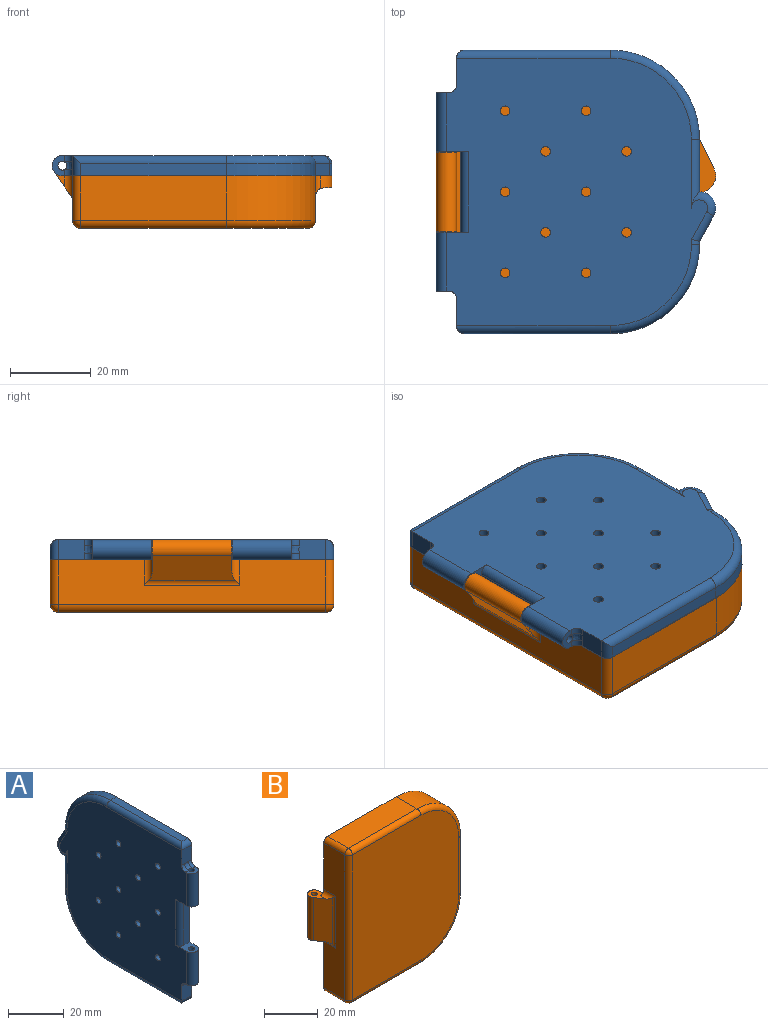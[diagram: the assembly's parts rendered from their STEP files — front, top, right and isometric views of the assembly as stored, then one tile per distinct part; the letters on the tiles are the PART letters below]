
ASSEMBLY  parts=2 mates=1
PART A: 78 faces, bbox 5.4x69.3x73.6 mm
  f0: plane 13x3mm, normal (0,1,0), area 39mm2, adj f1,f10,f59,f67
  f1: plane 70x66.5mm, normal (1,0,0), area 587.2mm2, adj f0,f3,f4,f5,f8,f9,f10,f11
  f2: plane 66x64.5mm, normal (-1,0,0), area 3648.1mm2, adj f3,f4,f40,f41,f42,f43,f44,f45
  f3: cylinder r=2.5mm len=14.5mm, axis (0,0,1), area 113.9mm2, adj f1,f2,f50,f54
  f4: cylinder r=2.5mm len=14.5mm, axis (0,0,1), area 113.9mm2, adj f1,f2,f51,f56
  f5: plane 3x1mm, normal (0,-1,0), area 3mm2, adj f1,f16,f21,f33
  f6: plane 62x52mm, normal (1,0,0), area 2899.7mm2, adj f7,f19,f20,f21,f22,f23,f24,f35
  f7: cylinder r=2mm len=3mm, axis (0,0,1), area 9.4mm2, adj f6,f17,f19,f38
  f8: plane 36x3mm, normal (0,0,1), area 108mm2, adj f1,f12,f61,f62
  f9: plane 36x3mm, normal (0,0,-1), area 108mm2, adj f1,f10,f68,f70
  f10: cylinder r=22mm len=22mm, axis (1,0,0), area 103.7mm2, adj f0,f1,f9,f69
  f11: plane 3x0.74mm, normal (0,1,0), area 2.2mm2, adj f1,f12,f60,f64
  f12: cylinder r=22mm len=22mm, axis (1,0,0), area 103.7mm2, adj f1,f8,f11,f63
  f13: plane 36x1mm, normal (0,0,-1), area 36mm2, adj f1,f14,f18,f20
  f14: plane 66x1mm, normal (0,1,0), area 66mm2, adj f1,f13,f15,f22
  f15: plane 36x1mm, normal (0,0,1), area 36mm2, adj f1,f14,f16,f24
  f16: cylinder r=20mm len=20mm, axis (1,0,0), area 31.4mm2, adj f1,f5,f15,f23
  f17: plane 3x1mm, normal (0,-1,0), area 3mm2, adj f1,f7,f18,f39
  f18: cylinder r=20mm len=20mm, axis (1,0,0), area 31.4mm2, adj f1,f13,f17,f19
  f19: torus R=18mm, axis (1,0,0), area 95.1mm2, adj f6,f7,f18,f20
  f20: cylinder r=2mm len=36mm, axis (0,-1,0), area 110.8mm2, adj f6,f13,f19,f22
  f21: cylinder r=2mm len=3mm, axis (0,0,1), area 9.4mm2, adj f5,f6,f23,f34
  f22: cylinder r=2mm len=66mm, axis (0,0,-1), area 202.8mm2, adj f6,f14,f20,f24
  f23: torus R=18mm, axis (1,0,0), area 95.1mm2, adj f6,f16,f21,f24
  f24: cylinder r=2mm len=36mm, axis (0,1,0), area 110.8mm2, adj f6,f15,f22,f23
  f25: plane 5x1mm, normal (0,0,-1), area 5mm2, adj f1,f26,f33,f35
  f26: plane 16x1mm, normal (0,-1,0), area 16mm2, adj f1,f25,f27,f36
  f27: plane 5x1mm, normal (0,0,1), area 5mm2, adj f1,f26,f37,f39
  f28: plane 6x3.5mm, normal (0,0,-1), area 21mm2, adj f1,f29,f31,f32
  f29: plane 13x3.5mm, normal (0,1,0), area 45.5mm2, adj f1,f28,f30,f32
  f30: plane 6x3.5mm, normal (0,0,1), area 21mm2, adj f1,f29,f31,f32
  f31: plane 13x3.5mm, normal (0,-1,0), area 45.5mm2, adj f1,f28,f30,f32
  f32: plane 13x6mm, normal (1,0,0), area 78mm2, adj f28,f29,f30,f31
  f33: cylinder r=2mm len=2mm, axis (-1,0,0), area 3.1mm2, adj f1,f5,f25,f34
  f34: sphere r=2mm, area 6.3mm2, adj f21,f33,f35
  f35: cylinder r=2mm len=7mm, axis (0,1,0), area 18mm2, adj f6,f25,f34,f36
  f36: cylinder r=2mm len=20mm, axis (0,0,-1), area 54.8mm2, adj f6,f26,f35,f37
  f37: cylinder r=2mm len=7mm, axis (0,-1,0), area 18mm2, adj f6,f27,f36,f38
  f38: sphere r=2mm, area 6.3mm2, adj f7,f37,f39
  f39: cylinder r=2mm len=2mm, axis (1,0,0), area 3.1mm2, adj f1,f17,f27,f38
  f40: cylinder r=1.2mm len=2.4mm, axis (1,0,0), area 15.1mm2, adj f2,f6
  f41: cylinder r=1.2mm len=2.4mm, axis (1,0,0), area 15.1mm2, adj f2,f6
  f42: cylinder r=1.2mm len=2.4mm, axis (1,0,0), area 15.1mm2, adj f2,f6
  f43: cylinder r=1.2mm len=2.4mm, axis (1,0,0), area 15.1mm2, adj f2,f6
  f44: cylinder r=1.2mm len=2.4mm, axis (1,0,0), area 15.1mm2, adj f2,f6
  f45: cylinder r=1.2mm len=2.4mm, axis (1,0,0), area 15.1mm2, adj f2,f6
  f46: cylinder r=1.2mm len=2.4mm, axis (1,0,0), area 15.1mm2, adj f2,f6
  f47: cylinder r=1.2mm len=2.4mm, axis (1,0,0), area 15.1mm2, adj f2,f6
  f48: cylinder r=1.2mm len=2.4mm, axis (1,0,0), area 15.1mm2, adj f2,f6
  f49: cylinder r=1.2mm len=2.4mm, axis (1,0,0), area 15.1mm2, adj f2,f6
  f50: plane 8x5mm, normal (0,0,1), area 24.4mm2, adj f1,f2,f3,f52,f58,f71
  f51: plane 8x5mm, normal (0,0,-1), area 24.4mm2, adj f1,f2,f4,f57,f58,f71
  f52: cylinder r=1.1mm len=14.5mm, axis (0,0,1), area 100.2mm2, adj f50,f54,f76
  f53: plane 6.59x5mm, normal (0,-1,0), area 32.6mm2, adj f1,f2,f68,f75,f76,f77
  f54: plane 5x3mm, normal (0,0,-1), area 9.4mm2, adj f1,f2,f3,f52,f75,f77
  f55: plane 6.59x5mm, normal (0,-1,0), area 32.6mm2, adj f1,f2,f61,f72,f73,f74
  f56: plane 5x3mm, normal (0,0,1), area 9.4mm2, adj f1,f2,f4,f57,f72,f74
  f57: cylinder r=1.1mm len=14.5mm, axis (0,0,1), area 100.2mm2, adj f51,f56,f73
  f58: plane 20x3mm, normal (0,-1,0), area 60mm2, adj f1,f50,f51,f71
  f59: cylinder r=4mm len=5.94mm, axis (1,0,0), area 24.9mm2, adj f0,f1,f60,f66
  f60: plane 6.32x3.5mm, normal (0,0.87,0.48), area 21.7mm2, adj f1,f11,f59,f65
  f61: cylinder r=2mm len=5mm, axis (-1,0,0), area 13.4mm2, adj f1,f8,f55,f62
  f62: cylinder r=2mm len=38mm, axis (0,1,0), area 117.1mm2, adj f2,f8,f61,f63
  f63: torus R=20mm, axis (1,0,0), area 105mm2, adj f2,f12,f62,f64
  f64: cylinder r=2mm len=2mm, axis (0,0,-1), area 3.1mm2, adj f2,f11,f63,f65
  f65: cylinder r=2mm len=7.74mm, axis (0,0.48,-0.87), area 23.5mm2, adj f2,f60,f64,f66
  f66: torus R=2mm, axis (1,0,0), area 23.8mm2, adj f2,f59,f65,f67
  f67: cylinder r=2mm len=17mm, axis (0,0,-1), area 43.8mm2, adj f0,f2,f66,f69
  f68: cylinder r=2mm len=5mm, axis (1,0,0), area 13.4mm2, adj f1,f9,f53,f70
  f69: torus R=20mm, axis (1,0,0), area 105mm2, adj f2,f10,f67,f70
  f70: cylinder r=2mm len=38mm, axis (0,-1,0), area 117.1mm2, adj f2,f9,f68,f69
  f71: cylinder r=2mm len=20mm, axis (0,0,1), area 62.8mm2, adj f2,f50,f51,f58
  f72: cylinder r=2mm len=2mm, axis (1,0,0), area 4.8mm2, adj f1,f55,f56,f73
  f73: bspline ~2x2mm, area 5.3mm2, adj f55,f57,f72,f74
  f74: cylinder r=2mm len=2mm, axis (1,0,0), area 4.8mm2, adj f2,f55,f56,f73
  f75: cylinder r=2mm len=2mm, axis (-1,0,0), area 4.8mm2, adj f1,f53,f54,f76
  f76: bspline ~2x2mm, area 5.3mm2, adj f52,f53,f75,f77
  f77: cylinder r=2mm len=2mm, axis (-1,0,0), area 4.8mm2, adj f2,f53,f54,f76
PART B: 62 faces, bbox 69x18x73.6 mm
  f0: plane 19.6x2.5mm, normal (1,0,0), area 49mm2, adj f3,f7,f41,f42
  f1: plane 36x11mm, normal (0,0,1), area 396mm2, adj f7,f13,f47,f48
  f2: plane 36x11mm, normal (0,0,-1), area 396mm2, adj f7,f11,f51,f56
  f3: cylinder r=2.5mm len=19.6mm, axis (0,0,1), area 183.1mm2, adj f0,f4,f41,f42
  f4: plane 21.35x6.23mm, normal (-0.83,-0.56,0), area 149mm2, adj f3,f41,f42,f59,f60,f61
  f5: plane 9x5mm, normal (0,0,1), area 37.9mm2, adj f6,f7,f34,f35,f37
  f6: plane 16x4mm, normal (-1,0,0), area 64mm2, adj f5,f7,f28,f34
  f7: plane 70x66mm, normal (0,1,0), area 536.5mm2, adj f0,f1,f2,f5,f6,f8,f10,f11
  f8: plane 9x3mm, normal (-1,0,0), area 27mm2, adj f7,f9,f18,f40
  f9: cylinder r=2mm len=3mm, axis (0,0,1), area 9.4mm2, adj f8,f21,f26,f39
  f10: plane 66x11mm, normal (-1,0,0), area 578.4mm2, adj f7,f47,f51,f52,f59,f60,f61
  f11: cylinder r=22mm len=22mm, axis (0,1,0), area 380.1mm2, adj f2,f7,f12,f45,f55
  f12: plane 26x11mm, normal (1,0,0), area 212.7mm2, adj f7,f11,f13,f53,f57,f58
  f13: cylinder r=22mm len=22mm, axis (0,1,0), area 380.1mm2, adj f1,f7,f12,f50
  f14: plane 66x56mm, normal (0,-1,0), area 3524.3mm2, adj f48,f50,f52,f53,f55,f56
  f15: plane 36x9mm, normal (0,0,-1), area 324mm2, adj f7,f16,f20,f23
  f16: plane 66x9mm, normal (1,0,0), area 594mm2, adj f7,f15,f17,f25
  f17: plane 36x9mm, normal (0,0,1), area 324mm2, adj f7,f16,f18,f27
  f18: cylinder r=20mm len=20mm, axis (0,1,0), area 282.7mm2, adj f7,f8,f17,f26
  f19: plane 9x3mm, normal (-1,0,0), area 27mm2, adj f7,f20,f24,f37
  f20: cylinder r=20mm len=20mm, axis (0,1,0), area 282.7mm2, adj f7,f15,f19,f22
  f21: plane 62x52mm, normal (0,1,0), area 3064.9mm2, adj f9,f22,f23,f24,f25,f26,f27,f34
  f22: torus R=18mm, axis (0,-1,0), area 95.1mm2, adj f20,f21,f23,f24
  f23: cylinder r=2mm len=36mm, axis (-1,0,0), area 110.8mm2, adj f15,f21,f22,f25
  f24: cylinder r=2mm len=3mm, axis (0,0,1), area 9.4mm2, adj f19,f21,f22,f36
  f25: cylinder r=2mm len=66mm, axis (0,0,-1), area 202.8mm2, adj f16,f21,f23,f27
  f26: torus R=18mm, axis (0,-1,0), area 95.1mm2, adj f9,f18,f21,f27
  f27: cylinder r=2mm len=36mm, axis (1,0,0), area 110.8mm2, adj f17,f21,f25,f26
  f28: plane 9x5mm, normal (0,0,-1), area 37.9mm2, adj f6,f7,f34,f38,f40
  f29: plane 6x3.5mm, normal (0,0,-1), area 21mm2, adj f7,f30,f32,f33
  f30: plane 13x3.5mm, normal (-1,0,0), area 45.5mm2, adj f7,f29,f31,f33
  f31: plane 6x3.5mm, normal (0,0,1), area 21mm2, adj f7,f30,f32,f33
  f32: plane 13x3.5mm, normal (1,0,0), area 45.5mm2, adj f7,f29,f31,f33
  f33: plane 13x6mm, normal (0,1,0), area 78mm2, adj f29,f30,f31,f32
  f34: plane 20x7mm, normal (-0.87,-0.5,0), area 131mm2, adj f5,f6,f21,f28,f35,f38
  f35: cylinder r=2mm len=2.14mm, axis (1,0,0), area 4.4mm2, adj f5,f21,f34,f36
  f36: sphere r=2mm, area 6.3mm2, adj f24,f35,f37
  f37: cylinder r=2mm len=9mm, axis (0,1,0), area 28.3mm2, adj f5,f7,f19,f36
  f38: cylinder r=2mm len=2.14mm, axis (-1,0,0), area 4.4mm2, adj f21,f28,f34,f39
  f39: sphere r=2mm, area 6.3mm2, adj f9,f38,f40
  f40: cylinder r=2mm len=9mm, axis (0,-1,0), area 28.3mm2, adj f7,f8,f28,f39
  f41: plane 7.69x5mm, normal (0,0,-1), area 19.9mm2, adj f0,f3,f4,f7,f43,f59
  f42: plane 7.69x5mm, normal (0,0,1), area 19.9mm2, adj f0,f3,f4,f7,f43,f61
  f43: cylinder r=1.1mm len=19.6mm, axis (0,0,1), area 135.5mm2, adj f41,f42
  f44: cylinder r=4mm len=5.55mm, axis (0,1,0), area 20.3mm2, adj f7,f45,f46,f57,f58
  f45: plane 7.22x5mm, normal (0.9,0,-0.44), area 26.1mm2, adj f7,f11,f44,f46,f57
  f46: plane 8.43x2mm, normal (0,-1,0), area 10.8mm2, adj f44,f45,f57
  f47: cylinder r=2mm len=11mm, axis (0,1,0), area 34.6mm2, adj f1,f7,f10,f49
  f48: cylinder r=2mm len=36mm, axis (1,0,0), area 113.1mm2, adj f1,f14,f49,f50
  f49: sphere r=2mm, area 6.3mm2, adj f47,f48,f52
  f50: torus R=20mm, axis (0,-1,0), area 105mm2, adj f13,f14,f48,f53
  f51: cylinder r=2mm len=11mm, axis (0,-1,0), area 34.6mm2, adj f2,f7,f10,f54
  f52: cylinder r=2mm len=66mm, axis (0,0,1), area 207.3mm2, adj f10,f14,f49,f54
  f53: cylinder r=2mm len=26mm, axis (0,0,-1), area 81.7mm2, adj f12,f14,f50,f55
  f54: sphere r=2mm, area 6.3mm2, adj f51,f52,f56
  f55: torus R=20mm, axis (0,-1,0), area 105mm2, adj f11,f14,f53,f56
  f56: cylinder r=2mm len=36mm, axis (-1,0,0), area 113.1mm2, adj f2,f14,f54,f55
  f57: cylinder r=2mm len=14.66mm, axis (0,0,-1), area 37.4mm2, adj f12,f44,f45,f46,f58
  f58: cylinder r=2mm len=5mm, axis (0,1,0), area 9.6mm2, adj f7,f12,f44,f57
  f59: cylinder r=2mm len=6.25mm, axis (0,1,0), area 14.6mm2, adj f4,f7,f10,f41,f60
  f60: cylinder r=2mm len=23.6mm, axis (0,0,1), area 26.8mm2, adj f4,f10,f59,f61
  f61: cylinder r=2mm len=6.25mm, axis (0,-1,0), area 14.6mm2, adj f4,f7,f10,f42,f60
PLACE A rot(axis=(0.58,0.58,-0.58),120deg) t=(-23.72,19.5,61.84)mm
PLACE B rot(axis=(1,0,0),90deg) t=(-30.22,19.45,61.84)mm
MATE revolute A.f3 <-> B.f3  axis (0,-1,0) through (-22.72,-5.5,64.34)mm
